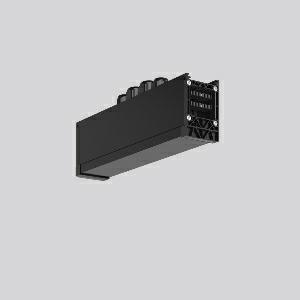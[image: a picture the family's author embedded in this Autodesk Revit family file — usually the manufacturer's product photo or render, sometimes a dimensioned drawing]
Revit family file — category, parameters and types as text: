
# Revit family: linedo_mitteleinspeisung_14pol_b_b_982698_013_1_032e
name_source: partatom
category: Lighting Fixtures
units: mm (PartAtom-declared; Revit-internal decimal feet)

## family parameters
Cut with Voids When Loaded = No
Host = Face
Light Source = No
Part Type = Normal
Room Calculation Point = No
Round Connector Dimension = Use Diameter
Shared = No

## types (1)
- LINEDO_Mitteleinspeisung_14pol_B_B
    Apparent Load = 0 VA
    Default Elevation = 1800 mm
    Description = Series: LINEDO
Middle power feed, 14-pole, connection socket / socket. Housing: extruded aluminium profile, powder-coated. Cover made of plastic, surface like housing. LINEDO plug system, plastic, black. 4 cable glands (2 x M20 and 2 x M25). Cable glands on top. Easy connection for rigid or flexible wires. Especially for use with continuous line modules with high opal diffuser.
Colour: black
Length: 312 mm
Width: 58 mm
Height: 91 mm
Weight: 900 g
    Height = 91 mm
    Lamp = 0 x
    Length = 312 mm
    Luminous efficacy = 0 lm/W
    Manufacturer = RZB
    ModVariant = No
    Model = 982698.013.1
    Mounting Place = Ceiling
    Mounting Type = Surface mounted
    Number of Poles = 1
    OnlyDefault = Yes
    Power Factor = 1
    Product Name = LINEDO_Mitteleinspeisung_14pol_B_B
    Product group = Surface mounted continuous line luminaire system
    ProductGroupID = 310
    Protection Class = Protection class I
    Protection Degree = Degree of protection
    RLX_Detail_Level = 1
    RLX_Emergency_Light_Flux = 0 lm
    RLX_Emergency_Type = 0
    RLX_Emergency_Type_DB = No
    RlxData = <blob elided: 24653 chars, md5=4c78d8ae>
    Standby Power = 0 W
    System Light Flux = 0 lm
    System Power = 0 W
    Type Comments = Product without accessories
    Type Image = 982698.013.1.jpg
    URL = http://relux.com
    VarID = ---
    Voltage = 0 V
    Weight = 0.00 kg
    Width = 58 mm

## geometry (parser evidence)
native form markers: Blend x4, Sweep x10
no freeform markers — native parametric forms only
